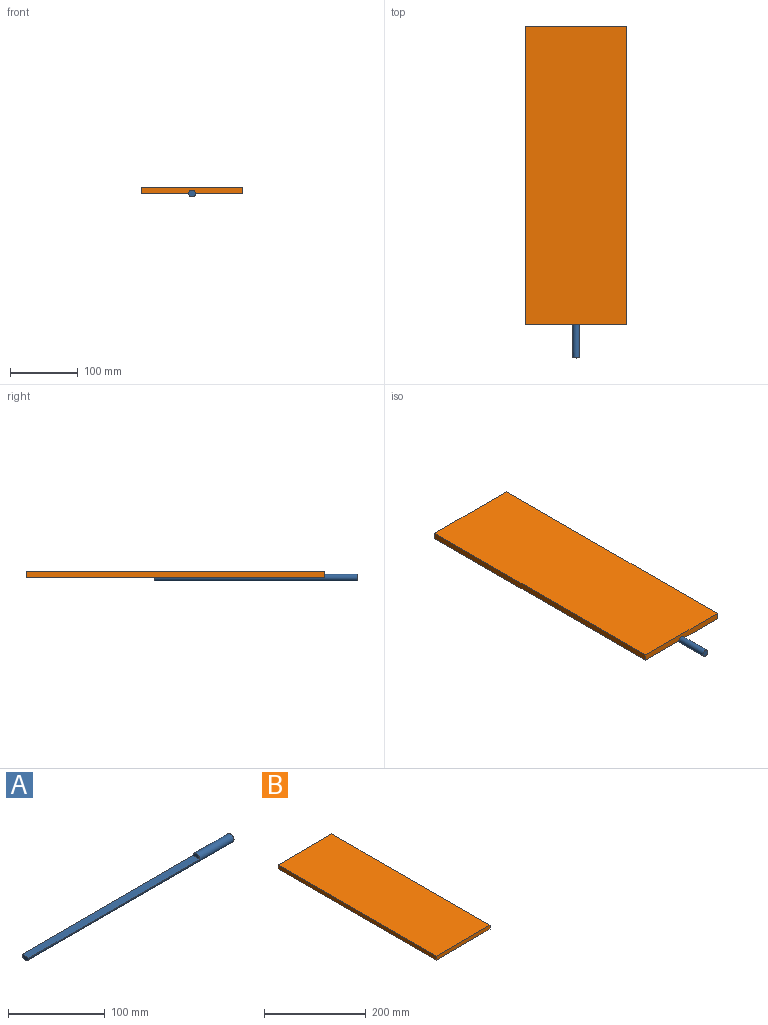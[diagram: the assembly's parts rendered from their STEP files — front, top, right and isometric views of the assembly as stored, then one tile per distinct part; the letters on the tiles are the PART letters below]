
ASSEMBLY  parts=2 mates=1
PART A: 5 faces, bbox 300x10x10 mm
  f0: cylinder r=5mm len=300mm, axis (-1,0,0), area 5497.8mm2, adj f1,f2,f3,f4
  f1: plane 10x10mm, normal (1,0,0), area 78.5mm2, adj f0
  f2: plane 10x5mm, normal (-1,0,0), area 39.3mm2, adj f0,f3
  f3: plane 250x10mm, normal (0,0,1), area 2500mm2, adj f0,f2,f4
  f4: plane 10x5mm, normal (-1,0,0), area 39.3mm2, adj f0,f3
PART B: 6 faces, bbox 150x440x9.5 mm
  f0: plane 440x9.53mm, normal (-1,0,0), area 4191mm2, adj f1,f3,f4,f5
  f1: plane 150x9.53mm, normal (0,-1,0), area 1428.7mm2, adj f0,f2,f4,f5
  f2: plane 440x9.53mm, normal (1,0,0), area 4191mm2, adj f1,f3,f4,f5
  f3: plane 150x9.53mm, normal (0,1,0), area 1428.7mm2, adj f0,f2,f4,f5
  f4: plane 440x150mm, normal (0,0,1), area 66000mm2, adj f0,f1,f2,f3
  f5: plane 440x150mm, normal (0,0,-1), area 66000mm2, adj f0,f1,f2,f3
PLACE A rot(axis=(0,0,-1),90deg) t=(-355.29,141.5,169.76)mm
PLACE B t=(-430.29,141.5,169.76)mm
MATE fastened A.f3 <-> B.f5  axis (0,0,1) through (-355.29,141.5,169.76)mm
